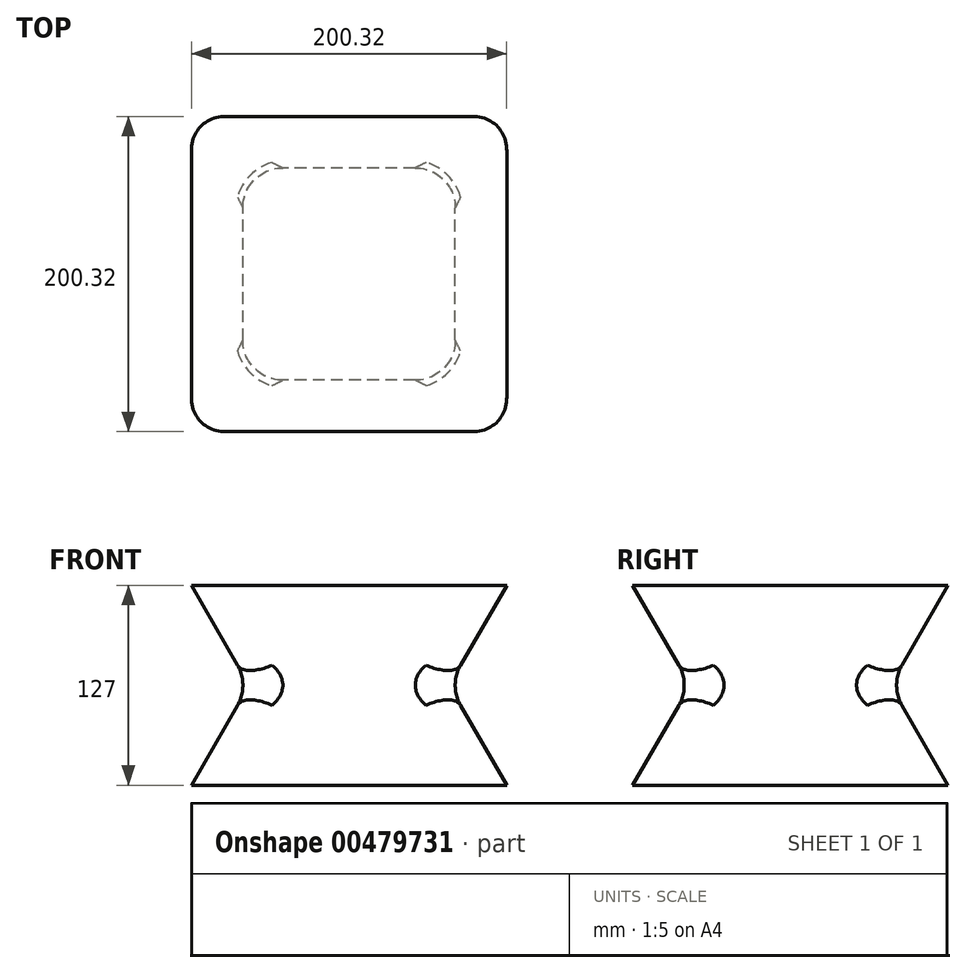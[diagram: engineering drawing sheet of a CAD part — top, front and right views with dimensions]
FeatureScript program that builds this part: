
annotation { "Feature Type Name" : "Feature", "Feature Type Description" : "" }
export const myFeature = defineFeature(function(context is Context, id is Id, definition is map)
    precondition{}
    {
        {
            var Q0;
            Q0=qCreatedBy(makeId("Top.planeOp"),FACE);
            var sketch = newSketch(context, id + "F0", { "sketchPlane" : qUnion([Q0])});
            skLineSegment(sketch, "E0.bottom", {"start": v(-63.5, 63.5) * mm, "end": v(63.5, 63.5) * mm});
            skLineSegment(sketch, "E0.top", {"start": v(-63.5, -63.5) * mm, "end": v(63.5, -63.5) * mm});
            skLineSegment(sketch, "E0.left", {"start": v(-63.5, 63.5) * mm, "end": v(-63.5, -63.5) * mm});
            skLineSegment(sketch, "E0.right", {"start": v(63.5, 63.5) * mm, "end": v(63.5, -63.5) * mm});
            skLineSegment(sketch, "E1", {"start": v(-63.5, 0) * mm, "end": v(63.5, 0) * mm, "construction": true});
            skPoint(sketch, "E2", {"position": v(0, 0) * mm});
            skSolve(sketch);
        }
        {
            var Q0;
            Q0=makeQuery(id+"F0.imprint","IMPRINT",FACE,{"disambiguationData":[TD([[makeQuery(id+"F0.imprint","IMPRINT",EDGE,{"derivedFrom":sQuery(id+"F0.wireOp",EDGE,"E0.bottom")}),-1.0]])]});
            extrude(context, id + "F1", {"entities" : qUnion([Q0]), "endBound" : BoundingType.SYMMETRIC, "depth" : 127 * mm, "hasDraft" : true, "draftAngle" : 30 * degree});
        }
        {
            var Q0;
            {var subQ0=makeQuery(id+"F1.opExtrude","SWEPT_FACE",FACE,{"disambiguationData":[OSD([sQuery(id+"F0.wireOp",EDGE,"E0.bottom")])]});Q0=makeQuery(id+"F1.*.booleanUnion.opBoolean","MERGE",EDGE,{"derivedFrom":[makeQuery(id+"F1.*.split.splitOp","SPLIT_SURFACE_INTERSECT",EDGE,{"derivedFrom":[subQ0]}),makeQuery(id+"F1.*.split.splitOp","SPLIT_SURFACE_INTERSECT",EDGE,{"derivedFrom":[subQ0],"isFromBackBody":true})]});}
            var Q1;
            {var subQ0=makeQuery(id+"F1.opExtrude","SWEPT_FACE",FACE,{"disambiguationData":[OSD([sQuery(id+"F0.wireOp",EDGE,"E0.right")])]});Q1=makeQuery(id+"F1.*.booleanUnion.opBoolean","MERGE",EDGE,{"derivedFrom":[makeQuery(id+"F1.*.split.splitOp","SPLIT_SURFACE_INTERSECT",EDGE,{"derivedFrom":[subQ0]}),makeQuery(id+"F1.*.split.splitOp","SPLIT_SURFACE_INTERSECT",EDGE,{"derivedFrom":[subQ0],"isFromBackBody":true})]});}
            var Q2;
            {var subQ0=makeQuery(id+"F1.opExtrude","SWEPT_FACE",FACE,{"disambiguationData":[OSD([sQuery(id+"F0.wireOp",EDGE,"E0.top")])]});Q2=makeQuery(id+"F1.*.booleanUnion.opBoolean","MERGE",EDGE,{"derivedFrom":[makeQuery(id+"F1.*.split.splitOp","SPLIT_SURFACE_INTERSECT",EDGE,{"derivedFrom":[subQ0]}),makeQuery(id+"F1.*.split.splitOp","SPLIT_SURFACE_INTERSECT",EDGE,{"derivedFrom":[subQ0],"isFromBackBody":true})]});}
            var Q3;
            {var subQ0=makeQuery(id+"F1.opExtrude","SWEPT_FACE",FACE,{"disambiguationData":[OSD([sQuery(id+"F0.wireOp",EDGE,"E0.left")])]});Q3=makeQuery(id+"F1.*.booleanUnion.opBoolean","MERGE",EDGE,{"derivedFrom":[makeQuery(id+"F1.*.split.splitOp","SPLIT_SURFACE_INTERSECT",EDGE,{"derivedFrom":[subQ0]}),makeQuery(id+"F1.*.split.splitOp","SPLIT_SURFACE_INTERSECT",EDGE,{"derivedFrom":[subQ0],"isFromBackBody":true})]});}
            fillet(context, id + "F2", {"entities" : qUnion([Q0, Q1, Q2, Q3]), "radius" : 25.4 * mm, "tangentPropagation" : true, "allowEdgeOverflow" : false});
        }
        {
            var Q0;
            Q0=makeQuery(id+"F1.*.split.splitOp","SPLIT",EDGE,{"derivedFrom":makeQuery(id+"F1.opExtrude","SWEPT_EDGE",EDGE,{"disambiguationData":[OSD([sQuery(id+"F0.wireOp",EDGE,"E0.bottom"),sQuery(id+"F0.wireOp",EDGE,"E0.right")])]}),"isFromBackBody":true});
            var Q1;
            Q1=makeQuery(id+"F1.*.split.splitOp","SPLIT",EDGE,{"derivedFrom":makeQuery(id+"F1.opExtrude","SWEPT_EDGE",EDGE,{"disambiguationData":[OSD([sQuery(id+"F0.wireOp",EDGE,"E0.top"),sQuery(id+"F0.wireOp",EDGE,"E0.right")])]}),"isFromBackBody":true});
            var Q2;
            Q2=makeQuery(id+"F1.*.split.splitOp","SPLIT",EDGE,{"derivedFrom":makeQuery(id+"F1.opExtrude","SWEPT_EDGE",EDGE,{"disambiguationData":[OSD([sQuery(id+"F0.wireOp",EDGE,"E0.top"),sQuery(id+"F0.wireOp",EDGE,"E0.left")])]}),"isFromBackBody":true});
            var Q3;
            Q3=makeQuery(id+"F1.*.split.splitOp","SPLIT",EDGE,{"derivedFrom":makeQuery(id+"F1.opExtrude","SWEPT_EDGE",EDGE,{"disambiguationData":[OSD([sQuery(id+"F0.wireOp",EDGE,"E0.bottom"),sQuery(id+"F0.wireOp",EDGE,"E0.left")])]}),"isFromBackBody":true});
            fillet(context, id + "F3", {"entities" : qUnion([Q0, Q1, Q2, Q3]), "radius" : 25.4 * mm, "tangentPropagation" : true, "allowEdgeOverflow" : false});
        }
    });
